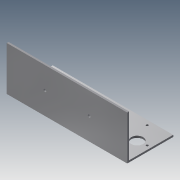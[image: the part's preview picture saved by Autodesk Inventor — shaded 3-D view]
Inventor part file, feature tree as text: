
AUTODESK INVENTOR PART (.ipt)
format: ipt  version: 2013 (Build 170138000, 138)  size: 160,256 bytes
history: native  units: mm
features: sketch x9, extrude x6, hole x3
ambient origin geometry x8: Origin, YZ Plane, XZ Plane, XY Plane, X Axis, Y Axis, Z Axis, Center Point
bodies: Solid1 (feature_tree)
feature tree (18):
  extrude  "Extrusion1"  Depth=7.0mm
  hole  "Hole1"  [1 undecoded]
  hole  "Hole2"  [1 undecoded]
  hole  "Hole4"  [1 undecoded]
  extrude  "Extrusion3"  Depth=2.4mm
  extrude  "Extrusion4"  Depth=7.0mm
  extrude  "Extrusion6"  Depth=31.0mm
  extrude  "Extrusion7"  Depth=25.0mm
  extrude  "Extrusion8"  TaperAngle=180.0deg  [1 undecoded]
  sketch  "Sketch1"  dims[d11=131.0mm d12=0.0mm d17=7.0mm]
  sketch  "Sketch2"  dims[d18=7.0mm]
  sketch  "Sketch3"  dims[d19=7.0mm d20=6.0mm d21=4.0mm d22=2.0mm d23=90.0deg d24=2.0mm d25=0.0mm d26=51.3mm]
  sketch  "Sketch5"  dims[d27=51.3mm d28=19.0mm]
  sketch  "Sketch7"  dims[d29=3.5mm d30=3.5mm]
  sketch  "Sketch8"  dims[d31=3.5mm d32=6.0mm d33=4.0mm d34=2.0mm d35=90.0deg d36=2.0mm d37=0.0mm d62=2.4mm]
  sketch  "Sketch9"  dims[d63=2.4mm]
  sketch  "Sketch11"  dims[d64=3.0mm d65=2.0mm d66=4.0mm d67=2.0mm d68=90.0deg d69=2.0mm d70=0.0mm d89=7.0mm]
  sketch  "Sketch12"  dims[d90=2.0mm d91=0.0mm d96=31.0mm d97=25.0mm d98=180.0deg d99=50.0mm d100=2.4mm d101=2.4mm d104=2.4mm d105=2.4mm d106=2.4mm d107=2.4mm d108=2.0mm d109=0.0mm d112=2.0mm d113=0.0mm d114=2.0mm d115=0.0mm d116=13.0mm d117=13.0mm d118=2.0mm d119=0.0mm]
note: 4 required parameter values undecoded (feature->parameter linkage not recoverable at this tier; creation-order binding heuristic only, values carry confidence <= 0.55)
